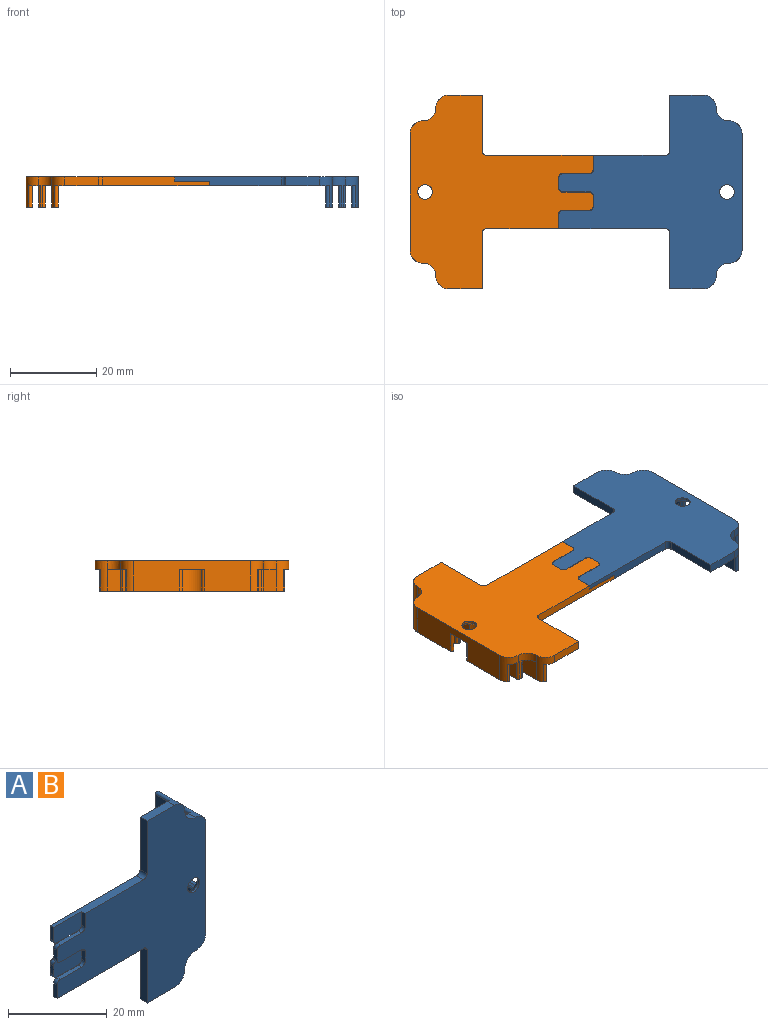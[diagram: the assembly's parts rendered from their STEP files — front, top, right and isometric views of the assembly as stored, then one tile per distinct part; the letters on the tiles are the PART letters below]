
ASSEMBLY  parts=2 mates=1
PART A: 85 faces, bbox 42.5x7x45 mm
  f0: plane 45x35.9mm, normal (0,1,0), area 786.7mm2, adj f10,f15,f16,f17,f18,f19,f20,f21
  f1: plane 39x7.1mm, normal (0,1,0), area 93.4mm2, adj f2,f4,f7,f9,f11,f24,f25,f26
  f2: plane 27x7mm, normal (1,0,0), area 161.1mm2, adj f1,f3,f5,f6,f63,f66,f77,f83
  f3: plane 45x42.5mm, normal (0,-1,0), area 1039.1mm2, adj f2,f15,f16,f17,f18,f19,f20,f21
  f4: plane 11.75x5mm, normal (-1,0,0), area 58.8mm2, adj f1,f5,f69,f84
  f5: plane 13.21x1.5mm, normal (0,1,0), area 18.9mm2, adj f2,f4,f24,f66,f69,f83,f84
  f6: plane 13.21x1.5mm, normal (0,1,0), area 18.9mm2, adj f2,f25,f26,f63,f70,f77,f78
  f7: plane 12.08x5mm, normal (-1,0,0), area 60.4mm2, adj f1,f8,f73,f79
  f8: plane 13.08x1.5mm, normal (0,1,0), area 19.3mm2, adj f7,f31,f32,f64,f73,f75,f79,f80
  f9: plane 16.91x5mm, normal (1,0,0), area 84.5mm2, adj f1,f12,f33,f68
  f10: plane 42x5mm, normal (-1,0,0), area 210mm2, adj f0,f12,f72,f74
  f11: plane 16.91x5mm, normal (1,0,0), area 84.5mm2, adj f1,f12,f33,f65
  f12: plane 43x1.5mm, normal (0,1,0), area 59.5mm2, adj f9,f10,f11,f33,f65,f68,f72,f74
  f13: plane 8x4.25mm, normal (0,-1,0), area 32.6mm2, adj f38,f39,f40,f55,f56,f57,f58,f59
  f14: plane 8x4.25mm, normal (0,-1,0), area 33.3mm2, adj f15,f46,f47,f50,f51,f52,f53
  f15: plane 24.7x2mm, normal (0,0,1), area 41.4mm2, adj f0,f3,f14,f23,f47,f50
  f16: plane 24.7x2mm, normal (0,0,-1), area 41.4mm2, adj f0,f3,f17,f35,f48,f62
  f17: cylinder r=1mm len=2mm, axis (0,1,0), area 3.1mm2, adj f0,f3,f16,f18
  f18: plane 13x2mm, normal (-1,0,0), area 26mm2, adj f0,f3,f17,f19
  f19: plane 7.8x2mm, normal (0,0,-1), area 15.6mm2, adj f0,f3,f18,f68
  f20: plane 7.8x2mm, normal (0,0,1), area 15.6mm2, adj f0,f3,f21,f65
  f21: plane 13x2mm, normal (-1,0,0), area 26mm2, adj f0,f3,f20,f23
  f22: cylinder r=1.7mm len=3.4mm, axis (0,1,0), area 5.3mm2, adj f3,f34
  f23: cylinder r=1mm len=2mm, axis (0,1,0), area 3.1mm2, adj f0,f3,f15,f21
  f24: cylinder r=3.6mm len=5mm, axis (0,-1,0), area 3mm2, adj f1,f5,f83,f84
  f25: cylinder r=3.6mm len=5mm, axis (0,-1,0), area 3mm2, adj f1,f6,f77,f78
  f26: plane 11.75x5mm, normal (-1,0,0), area 58.8mm2, adj f1,f6,f70,f78
  f27: plane 11.94x5mm, normal (1,0,0), area 59.7mm2, adj f1,f30,f76,f82
  f28: plane 12.08x5mm, normal (-1,0,0), area 60.4mm2, adj f1,f30,f71,f81
  f29: cylinder r=3.6mm len=5mm, axis (0,-1,0), area 2.2mm2, adj f1,f30,f81,f82
  f30: plane 13.08x1.5mm, normal (0,1,0), area 19.3mm2, adj f27,f28,f29,f67,f71,f76,f81,f82
  f31: plane 11.94x5mm, normal (1,0,0), area 59.7mm2, adj f1,f8,f75,f80
  f32: cylinder r=3.6mm len=5mm, axis (0,-1,0), area 2.2mm2, adj f1,f8,f79,f80
  f33: cylinder r=3.6mm len=5.18mm, axis (0,-1,0), area 28.9mm2, adj f1,f9,f11,f12
  f34: cone r=3.2mm half-angle=45deg, axis (0,1,0), area 32.7mm2, adj f1,f22
  f35: plane 3.3x1mm, normal (-1,0,0), area 3.3mm2, adj f3,f16,f36,f48
  f36: cylinder r=0.9mm len=1mm, axis (0,-1,0), area 1.4mm2, adj f3,f35,f37,f48
  f37: plane 6.1x1mm, normal (0,0,1), area 6.1mm2, adj f3,f36,f38,f48
  f38: cylinder r=1mm len=1mm, axis (0,-1,0), area 1.6mm2, adj f3,f13,f37,f39,f48
  f39: plane 2.35x1mm, normal (-1,0,0), area 2.3mm2, adj f3,f13,f38,f40
  f40: cylinder r=1mm len=1mm, axis (0,-1,0), area 1.6mm2, adj f3,f13,f39,f41,f49
  f41: plane 6.1x1mm, normal (0,0,-1), area 6.1mm2, adj f3,f40,f42,f49
  f42: cylinder r=0.9mm len=1mm, axis (0,-1,0), area 1.4mm2, adj f3,f41,f43,f49
  f43: plane 2.35x1mm, normal (-1,0,0), area 2.4mm2, adj f3,f42,f44,f49
  f44: cylinder r=0.9mm len=1mm, axis (0,-1,0), area 1.4mm2, adj f3,f43,f45,f49
  f45: plane 6.1x1mm, normal (0,0,1), area 6.1mm2, adj f3,f44,f46,f49
  f46: cylinder r=1mm len=1mm, axis (0,-1,0), area 1.6mm2, adj f3,f14,f45,f47,f49
  f47: plane 3.3x1mm, normal (-1,0,0), area 3.3mm2, adj f3,f14,f15,f46
  f48: plane 8x4.25mm, normal (0,1,0), area 33.3mm2, adj f16,f35,f36,f37,f38,f61,f62
  f49: plane 8x4.25mm, normal (0,1,0), area 32.6mm2, adj f40,f41,f42,f43,f44,f45,f46,f53
  f50: plane 3.3x1mm, normal (-1,0,0), area 3.3mm2, adj f0,f14,f15,f51
  f51: cylinder r=0.9mm len=1mm, axis (0,1,0), area 1.4mm2, adj f0,f14,f50,f52
  f52: plane 6.1x1mm, normal (0,0,-1), area 6.1mm2, adj f0,f14,f51,f53
  f53: cylinder r=1mm len=1mm, axis (0,1,0), area 1.6mm2, adj f0,f14,f49,f52,f54
  f54: plane 2.35x1mm, normal (-1,0,0), area 2.4mm2, adj f0,f49,f53,f55
  f55: cylinder r=1mm len=1mm, axis (0,1,0), area 1.6mm2, adj f0,f13,f49,f54,f56
  f56: plane 6.1x1mm, normal (0,0,1), area 6.1mm2, adj f0,f13,f55,f57
  f57: cylinder r=0.9mm len=1mm, axis (0,1,0), area 1.4mm2, adj f0,f13,f56,f58
  f58: plane 2.35x1mm, normal (-1,0,0), area 2.3mm2, adj f0,f13,f57,f59
  f59: cylinder r=0.9mm len=1mm, axis (0,1,0), area 1.4mm2, adj f0,f13,f58,f60
  f60: plane 6.1x1mm, normal (0,0,-1), area 6.1mm2, adj f0,f13,f59,f61
  f61: cylinder r=1mm len=1mm, axis (0,1,0), area 1.6mm2, adj f0,f13,f48,f60,f62
  f62: plane 3.3x1mm, normal (-1,0,0), area 3.3mm2, adj f0,f16,f48,f61
  f63: cylinder r=3mm len=7mm, axis (0,-1,0), area 19.1mm2, adj f1,f2,f3,f6,f64,f70
  f64: cylinder r=3mm len=7mm, axis (0,-1,0), area 11.6mm2, adj f1,f3,f8,f63,f65,f73,f75
  f65: cylinder r=3mm len=7mm, axis (0,-1,0), area 19.1mm2, adj f0,f3,f11,f12,f20,f64,f74
  f66: cylinder r=3mm len=7mm, axis (0,-1,0), area 19.1mm2, adj f1,f2,f3,f5,f67,f69
  f67: cylinder r=3mm len=7mm, axis (0,-1,0), area 11.6mm2, adj f1,f3,f30,f66,f68,f71,f76
  f68: cylinder r=3mm len=7mm, axis (0,-1,0), area 19.1mm2, adj f0,f3,f9,f12,f19,f67,f72
  f69: cylinder r=0.5mm len=5mm, axis (0,-1,0), area 6.2mm2, adj f1,f4,f5,f66
  f70: cylinder r=0.5mm len=5mm, axis (0,-1,0), area 6.2mm2, adj f1,f6,f26,f63
  f71: cylinder r=0.5mm len=5mm, axis (0,-1,0), area 4.7mm2, adj f1,f28,f30,f67
  f72: cylinder r=0.5mm len=5mm, axis (0,-1,0), area 6.2mm2, adj f0,f10,f12,f68
  f73: cylinder r=0.5mm len=5mm, axis (0,-1,0), area 4.7mm2, adj f1,f7,f8,f64
  f74: cylinder r=0.5mm len=5mm, axis (0,-1,0), area 6.2mm2, adj f0,f10,f12,f65
  f75: cylinder r=0.5mm len=5mm, axis (0,-1,0), area 3.6mm2, adj f1,f8,f31,f64
  f76: cylinder r=0.5mm len=5mm, axis (0,-1,0), area 3.6mm2, adj f1,f27,f30,f67
  f77: cylinder r=0.5mm len=5mm, axis (0,-1,0), area 6mm2, adj f1,f2,f6,f25
  f78: cylinder r=0.5mm len=5mm, axis (0,-1,0), area 2.3mm2, adj f1,f6,f25,f26
  f79: cylinder r=0.5mm len=5mm, axis (0,-1,0), area 4.2mm2, adj f1,f7,f8,f32
  f80: cylinder r=0.5mm len=5mm, axis (0,-1,0), area 3.9mm2, adj f1,f8,f31,f32
  f81: cylinder r=0.5mm len=5mm, axis (0,-1,0), area 4.2mm2, adj f1,f28,f29,f30
  f82: cylinder r=0.5mm len=5mm, axis (0,-1,0), area 3.9mm2, adj f1,f27,f29,f30
  f83: cylinder r=0.5mm len=5mm, axis (0,-1,0), area 6mm2, adj f1,f2,f5,f24
  f84: cylinder r=0.5mm len=5mm, axis (0,-1,0), area 2.3mm2, adj f1,f4,f5,f24
PART B: same geometry as A
PLACE A rot(axis=(-1,0,0),90deg) t=(-26.82,8.64,-2)mm
PLACE B rot(axis=(0,0.71,-0.71),180deg) t=(-18.67,-8.36,-2)mm
MATE fastened A.f48 <-> B.f14  axis (0,0,-1) through (-18.72,-8.36,-1)mm
